# Revit family: NAU_Naughtone_Tbls_Tun
name_source: partatom
category: Furniture
revit_build: Autodesk Revit 2018 (Build: 20170223_1515(x64)
units: mm (PartAtom-declared; Revit-internal decimal feet)

## family parameters
Always vertical = Yes
Cut with Voids When Loaded = No
OmniClass Number = 23.40.20.00
OmniClass Title = General Furniture and Specialties
Room Calculation Point = No
Shared = Yes
Work Plane-Based = No

## types (6) — shared parameters
Assembly Code = E2020200
AssetType = Movable
BIMObjectName = NAU_Naughtone_Tables_Tun
Category = Pr_40_50_21 : Desks, tables and worktops
Color = Black
DurationUnit = year
Finish = Black, white or RAL steel base
IfcExportAs = IfcFurnishingElementType
IfcExportType = TABLE
Keynote = Pr_40_50_21
MainColor = Black
ManufacturerAddress = Knaresborough Tech Park, Manse Lane, Knaresborough, HG5 8LF
ManufacturerName = Naughtone
ManufacturerURL = www.naughtone.com
Material = Top available in white or black MFMDF; oak or walnut veneer; or Forbo lino
NBSDescription = Tables
NBSReference = 45-35-86/327
Name = Tables_Tun_Naughtone
ProductInformation = www.naughtone.com/products/
Revision = 0
Shape = Rectangular
URL = www.naughtone.com
Uniclass2015Code = Pr_40_50_21
Uniclass2015Title = Desks, tables and worktops
Version = 1
WarrantyDescription = Request warranty information from naughtone
WarrantyDurationLabor = 7
WarrantyDurationParts = 7
WarrantyDurationUnit = year
zero-valued in all types: NumberOfChairs, WorksurfaceArea

## per-type parameters (varying)
| type | IsTUN420ST | IsTUN420UP | IsTUN620ST | IsTUN620UP | IsTUN920ST | IsTUN920UP | Model | ModelNumber | NominalHeight | NominalLength | NominalWidth | Radius | Size |
| Tun 920 Coffee Table Upholstered Base | No | No | No | No | No | Yes | TUN920UP | TUN920UP | 350 mm  [stored 1.14829 ft] | 916 mm | 566 mm  [stored 1.85696 ft] | 283 mm  [stored 0.928478 ft] | 916 x 566 x 350mm |
| Tun 920 Coffee Table Steel Base | No | No | No | No | Yes | No | TUN920ST | TUN920ST | 350 mm  [stored 1.14829 ft] | 916 mm | 566 mm  [stored 1.85696 ft] | 283 mm  [stored 0.928478 ft] | 916 x 566 x 350mm |
| Tun 620 Side Table Steel Base | No | No | Yes | No | No | No | TUN620ST | TUN620ST | 450 mm  [stored 1.47638 ft] | 622 mm  [stored 2.04068 ft] | 450 mm  [stored 1.47638 ft] | 225 mm  [stored 0.738189 ft] | 622 x 450 x 450mm |
| Tun 620 Side Table Upholstered Base | No | No | No | Yes | No | No | TUN620UP | TUN620UP | 450 mm  [stored 1.47638 ft] | 622 mm  [stored 2.04068 ft] | 450 mm  [stored 1.47638 ft] | 225 mm  [stored 0.738189 ft] | 622 x 450 x 450mm |
| Tun 420 Side Table Steel Base | Yes | No | No | No | No | No | TUN420ST | TUN420ST | 550 mm | 422 mm  [stored 1.38451 ft] | 340 mm  [stored 1.11549 ft] | 170 mm  [stored 0.557743 ft] | 422 x 340 x 550mm |
| Tun 420 Side Table Upholstered Base | No | Yes | No | No | No | No | TUN420UP | TUN420UP | 550 mm | 422 mm  [stored 1.38451 ft] | 340 mm  [stored 1.11549 ft] | 170 mm  [stored 0.557743 ft] | 422 x 340 x 550mm |

note: column(s) folded — value = type name in every type: Description, ModelReference

note: [stored X ft] marks values corroborated as IEEE doubles in the binary element streams (Revit-internal decimal feet)

## geometry (parser evidence)
native form markers: Sweep x4
no freeform markers — native parametric forms only
